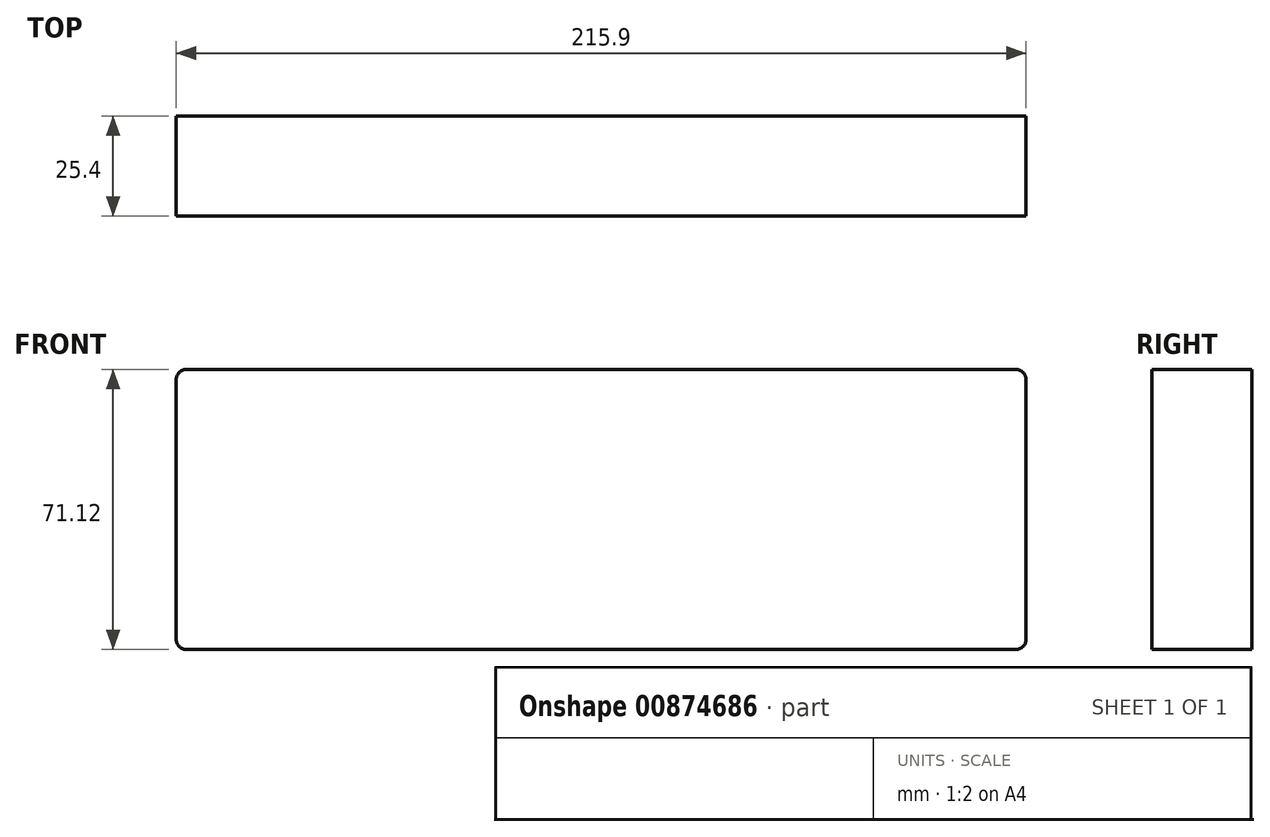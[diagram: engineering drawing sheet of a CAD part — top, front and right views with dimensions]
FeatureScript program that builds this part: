
annotation { "Feature Type Name" : "Feature", "Feature Type Description" : "" }
export const myFeature = defineFeature(function(context is Context, id is Id, definition is map)
    precondition{}
    {
        {
            var Q0;
            Q0=qCreatedBy(makeId("Front.planeOp"),FACE);
            var sketch = newSketch(context, id + "F0", { "sketchPlane" : qUnion([Q0])});
            skLineSegment(sketch, "E0.bottom", {"start": v(2.54, 0) * mm, "end": v(213.36, 0) * mm});
            skLineSegment(sketch, "E0.top", {"start": v(2.54, 71.12) * mm, "end": v(213.36, 71.12) * mm});
            skLineSegment(sketch, "E0.left", {"start": v(0, 2.54) * mm, "end": v(0, 68.58) * mm});
            skLineSegment(sketch, "E0.right", {"start": v(215.9, 2.54) * mm, "end": v(215.9, 68.58) * mm});
            skPoint(sketch, "E1.visualSharp", {"position": v(0, 71.12) * mm});
            skArc(sketch, "E1.filletArc", {"start": v(2.54, 71.12) * mm, "mid": v(0.74, 70.38) * mm, "end": v(0, 68.58) * mm});
            skPoint(sketch, "E2.visualSharp", {"position": v(0, 0) * mm});
            skArc(sketch, "E2.filletArc", {"start": v(0, 2.54) * mm, "mid": v(0.74, 0.74) * mm, "end": v(2.54, 0) * mm});
            skPoint(sketch, "E3.visualSharp", {"position": v(215.9, 0) * mm});
            skArc(sketch, "E3.filletArc", {"start": v(213.36, 0) * mm, "mid": v(215.16, 0.74) * mm, "end": v(215.9, 2.54) * mm});
            skPoint(sketch, "E4.visualSharp", {"position": v(215.9, 71.12) * mm});
            skArc(sketch, "E4.filletArc", {"start": v(215.9, 68.58) * mm, "mid": v(215.16, 70.38) * mm, "end": v(213.36, 71.12) * mm});
            skSolve(sketch);
        }
        {
            var Q0;
            Q0=makeQuery(id+"F0.imprint","IMPRINT",FACE,{"disambiguationData":[TD([[makeQuery(id+"F0.imprint","IMPRINT",EDGE,{"derivedFrom":sQuery(id+"F0.wireOp",EDGE,"E0.bottom")}),1.0]])]});
            extrude(context, id + "F1", {"entities" : qUnion([Q0]), "depth" : 25.4 * mm, "offsetDistance" : 25.4 * mm});
        }
    });
